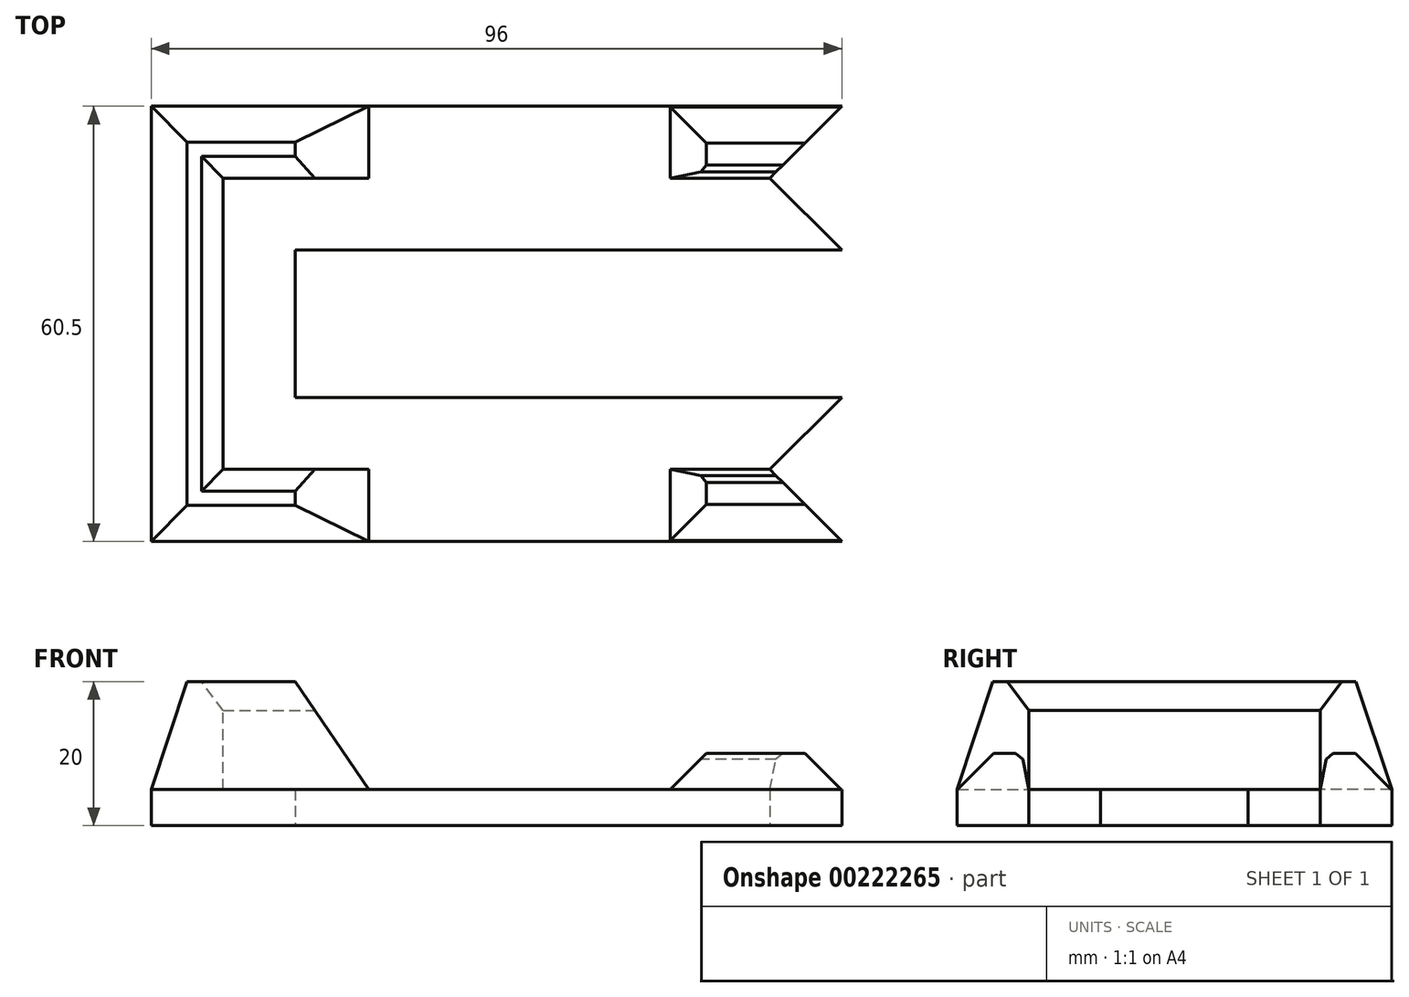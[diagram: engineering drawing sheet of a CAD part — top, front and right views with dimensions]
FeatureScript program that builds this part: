
annotation { "Feature Type Name" : "Feature", "Feature Type Description" : "" }
export const myFeature = defineFeature(function(context is Context, id is Id, definition is map)
    precondition{}
    {
        {
            var Q0;
            Q0=qCreatedBy(makeId("Top.planeOp"),FACE);
            var sketch = newSketch(context, id + "F0", { "sketchPlane" : qUnion([Q0])});
            skLineSegment(sketch, "E0.bottom", {"start": v(76, -20.25) * mm, "end": v(-76, -20.25) * mm, "construction": true});
            skLineSegment(sketch, "E0.top", {"start": v(76, 20.25) * mm, "end": v(-76, 20.25) * mm, "construction": true});
            skLineSegment(sketch, "E0.left", {"start": v(76, -20.25) * mm, "end": v(76, 20.25) * mm, "construction": true});
            skLineSegment(sketch, "E0.right", {"start": v(-76, -20.25) * mm, "end": v(-76, 20.25) * mm, "construction": true});
            skPoint(sketch, "E0.middle", {"position": v(0, 0) * mm});
            skLineSegment(sketch, "E1.bottom", {"start": v(86, -30.25) * mm, "end": v(-86, -30.25) * mm});
            skLineSegment(sketch, "E1.top", {"start": v(86, 30.25) * mm, "end": v(-86, 30.25) * mm});
            skLineSegment(sketch, "E1.left", {"start": v(86, -30.25) * mm, "end": v(86, 30.25) * mm});
            skLineSegment(sketch, "E1.right", {"start": v(-86, -30.25) * mm, "end": v(-86, 30.25) * mm});
            skSolve(sketch);
        }
        {
            var Q0;
            Q0=qCreatedBy(makeId("Top.planeOp"),FACE);
            cPlane(context, id + "F1", {"entities" : qUnion([Q0]), "cplaneType" : CPlaneType.OFFSET, "offset" : 15 * mm, "width" : 150 * mm, "height" : 150 * mm});
        }
        {
            var Q0;
            Q0=qCreatedBy(id+"F1.planeOp",FACE);
            var sketch = newSketch(context, id + "F2", { "sketchPlane" : qUnion([Q0])});
            skPoint(sketch, "E2.0", {"position": v(-86, -30.25) * mm});
            skPoint(sketch, "E3.0", {"position": v(-76, -20.25) * mm});
            skLineSegment(sketch, "E4", {"start": v(-76, 0) * mm, "end": v(-76, -20.25) * mm});
            skLineSegment(sketch, "E5", {"start": v(-76, -20.25) * mm, "end": v(-86, -30.25) * mm, "construction": true});
            skPoint(sketch, "E6", {"position": v(-81, -25.25) * mm});
            skLineSegment(sketch, "E7", {"start": v(-76, 0) * mm, "end": v(-81, 0) * mm});
            skLineSegment(sketch, "E8", {"start": v(-81, 0) * mm, "end": v(-81, -25.25) * mm});
            skLineSegment(sketch, "E9", {"start": v(-76, -20.25) * mm, "end": v(-66, -20.25) * mm});
            skLineSegment(sketch, "E10", {"start": v(-66, -20.25) * mm, "end": v(-66, -25.25) * mm});
            skLineSegment(sketch, "E11", {"start": v(-66, -25.25) * mm, "end": v(-81, -25.25) * mm});
            skSolve(sketch);
        }
        {
            var Q0;
            Q0=qCreatedBy(makeId("Top.planeOp"),FACE);
            var sketch = newSketch(context, id + "F3", { "sketchPlane" : qUnion([Q0])});
            skPoint(sketch, "E12.0", {"position": v(-86, -30.25) * mm});
            skPoint(sketch, "E13.0", {"position": v(-76, -20.25) * mm});
            skLineSegment(sketch, "E14", {"start": v(-86, -30.25) * mm, "end": v(-86, 0) * mm});
            skLineSegment(sketch, "E15", {"start": v(-86, 0) * mm, "end": v(-76, 0) * mm});
            skLineSegment(sketch, "E16", {"start": v(-76, 0) * mm, "end": v(-76, -20.25) * mm});
            skLineSegment(sketch, "E17", {"start": v(-76, -20.25) * mm, "end": v(-86, -30.25) * mm, "construction": true});
            skLineSegment(sketch, "E18.MirrorCS", {"start": v(-55.75, -20.25) * mm, "end": v(-76, -20.25) * mm});
            skLineSegment(sketch, "E19.MirrorCS", {"start": v(-86, -30.25) * mm, "end": v(-55.75, -30.25) * mm});
            skLineSegment(sketch, "E20.MirrorCS", {"start": v(-55.75, -30.25) * mm, "end": v(-55.75, -20.25) * mm});
            skLineSegment(sketch, "E21", {"start": v(0, 0) * mm, "end": v(-88.2, 0) * mm, "construction": true});
            skSolve(sketch);
        }
        {
            var Q0;
            Q0=makeQuery(id+"F0.imprint","IMPRINT",FACE,{"disambiguationData":[TD([[makeQuery(id+"F0.imprint","IMPRINT",EDGE,{"derivedFrom":sQuery(id+"F0.wireOp",EDGE,"E1.bottom")}),-1.0]])]});
            extrude(context, id + "F4", {"entities" : qUnion([Q0]), "oppositeDirection" : true, "depth" : 5 * mm});
        }
        {
            var Q1;
            Q1=makeQuery(id+"F3.imprint","IMPRINT",FACE,{"disambiguationData":[TD([[makeQuery(id+"F3.imprint","IMPRINT",EDGE,{"derivedFrom":sQuery(id+"F3.wireOp",EDGE,"E14")}),-1.0]])]});
            var Q2;
            Q2=makeQuery(id+"F2.imprint","IMPRINT",FACE,{"disambiguationData":[TD([[makeQuery(id+"F2.imprint","IMPRINT",EDGE,{"derivedFrom":sQuery(id+"F2.wireOp",EDGE,"E4")}),-1.0]])]});
            loft(context, id + "F5", {"operationType" : NewBodyOperationType.ADD, "sheetProfilesArray" : [{ "sheetProfileEntities" : qUnion([Q1]) }, { "sheetProfileEntities" : qUnion([Q2]) }]});
        }
        {
            var Q0;
            Q0=makeQuery(id+"F5.opLoft","MID_CAP_EDGE",EDGE,{"disambiguationData":[OSD([sQuery(id+"F2.wireOp",EDGE,"E4"),sQuery(id+"F2.wireOp",EDGE,"E7"),sQuery(id+"F2.wireOp",EDGE,"E9")])],"capPos":1.0});
            var Q1;
            Q1=makeQuery(id+"F5.opLoft","MID_CAP_EDGE",EDGE,{"disambiguationData":[OSD([sQuery(id+"F2.wireOp",EDGE,"E4"),sQuery(id+"F2.wireOp",EDGE,"E9"),sQuery(id+"F2.wireOp",EDGE,"E10")])],"capPos":1.0});
            chamfer(context, id + "F6", {"entities" : qUnion([Q0, Q1]), "chamferType" : ChamferType.TWO_OFFSETS, "width1" : 3 * mm, "oppositeDirection" : false, "width2" : 4 * mm, "tangentPropagation" : true});
        }
        {
            var Q0;
            Q0=makeQuery(id+"F4.opExtrude","SWEPT_BODY",BODY,{"disambiguationData":[OSD([sQuery(id+"F0.wireOp",EDGE,"E1.bottom"),sQuery(id+"F0.wireOp",EDGE,"E1.top"),sQuery(id+"F0.wireOp",EDGE,"E1.left"),sQuery(id+"F0.wireOp",EDGE,"E1.right")])]});
            var Q1;
            Q1=qCreatedBy(makeId("Right.planeOp"),FACE);
            mirror(context, id + "F7", {"operationType" : NewBodyOperationType.ADD, "entities" : qUnion([Q0]), "mirrorPlane" : qUnion([Q1])});
        }
        {
            var Q0;
            Q0=makeQuery(id+"F0.imprint","IMPRINT",FACE,{"disambiguationData":[TD([[makeQuery(id+"F0.imprint","IMPRINT",EDGE,{"derivedFrom":sQuery(id+"F0.wireOp",EDGE,"E1.bottom")}),-1.0]])]});
            var sketch = newSketch(context, id + "F8", { "sketchPlane" : qUnion([Q0])});
            skLineSegment(sketch, "E22", {"start": v(0, 45.4) * mm, "end": v(0, -36.03) * mm, "construction": true});
            skLineSegment(sketch, "E23", {"start": v(0, -20.25) * mm, "end": v(13.82, -20.25) * mm});
            skLineSegment(sketch, "E24", {"start": v(13.82, -20.25) * mm, "end": v(13.82, -30.13) * mm});
            skLineSegment(sketch, "E25", {"start": v(13.82, -30.13) * mm, "end": v(0, -30.13) * mm});
            skLineSegment(sketch, "E26.MirrorCS", {"start": v(-13.82, -30.13) * mm, "end": v(0, -30.13) * mm});
            skLineSegment(sketch, "E27.MirrorCS", {"start": v(0, -20.25) * mm, "end": v(-13.82, -20.25) * mm});
            skLineSegment(sketch, "E28.MirrorCS", {"start": v(-13.82, -20.25) * mm, "end": v(-13.82, -30.13) * mm});
            skSolve(sketch);
        }
        {
            var Q0;
            Q0=qSketchRegion(id+"F8",true);
            extrude(context, id + "F9", {"entities" : qUnion([Q0]), "operationType" : NewBodyOperationType.ADD, "depth" : 5 * mm});
        }
        {
            var Q0;
            Q0=makeQuery(id+"F9.opExtrude","CAP_EDGE",EDGE,{"disambiguationData":[OSD([sQuery(id+"F8.wireOp",EDGE,"E24")])],"isStart":false});
            var Q1;
            Q1=makeQuery(id+"F9.opExtrude","CAP_EDGE",EDGE,{"disambiguationData":[OSD([sQuery(id+"F8.wireOp",EDGE,"E25"),sQuery(id+"F8.wireOp",EDGE,"E26.MirrorCS")])],"isStart":false});
            var Q2;
            Q2=makeQuery(id+"F9.opExtrude","CAP_EDGE",EDGE,{"disambiguationData":[OSD([sQuery(id+"F8.wireOp",EDGE,"E28.MirrorCS")])],"isStart":false});
            chamfer(context, id + "F10", {"entities" : qUnion([Q0, Q1, Q2]), "width" : 5 * mm, "tangentPropagation" : true});
        }
        {
            var Q0;
            Q0=makeQuery(id+"F9.opExtrude","CAP_EDGE",EDGE,{"disambiguationData":[OSD([sQuery(id+"F8.wireOp",EDGE,"E23"),sQuery(id+"F8.wireOp",EDGE,"E27.MirrorCS")])],"isStart":false});
            chamfer(context, id + "F11", {"entities" : qUnion([Q0]), "chamferType" : ChamferType.TWO_OFFSETS, "width1" : 5 * mm, "oppositeDirection" : false, "width2" : 1 * mm, "tangentPropagation" : true});
        }
        {
            var Q0;
            {var subQ0=sQuery(id+"F8.wireOp",EDGE,"E27.MirrorCS");var subQ1=sQuery(id+"F8.wireOp",EDGE,"E23");Q0=makeQuery(id+"F11.opChamfer","BLEND_EDGE",EDGE,{"blendedFrom":[makeQuery(id+"F9.opExtrude","CAP_EDGE",EDGE,{"disambiguationData":[OSD([subQ1,subQ0])],"isStart":false}),makeQuery(id+"F9.opExtrude","CAP_FACE",FACE,{"disambiguationData":[OSD([subQ1,sQuery(id+"F8.wireOp",EDGE,"E24"),sQuery(id+"F8.wireOp",EDGE,"E25"),subQ0,sQuery(id+"F8.wireOp",EDGE,"E28.MirrorCS"),sQuery(id+"F8.wireOp",EDGE,"E26.MirrorCS")])],"isStart":false})],"blendedInto":[makeQuery(id+"F9.opExtrude","CAP_FACE",FACE,{"disambiguationData":[OSD([subQ1,sQuery(id+"F8.wireOp",EDGE,"E24"),sQuery(id+"F8.wireOp",EDGE,"E25"),subQ0,sQuery(id+"F8.wireOp",EDGE,"E28.MirrorCS"),sQuery(id+"F8.wireOp",EDGE,"E26.MirrorCS")])],"isStart":false})]});}
            chamfer(context, id + "F12", {"entities" : qUnion([Q0]), "width" : 1 * mm, "tangentPropagation" : true});
        }
        {
            var Q0;
            Q0=makeQuery(id+"F4.opExtrude","SWEPT_BODY",BODY,{"disambiguationData":[OSD([sQuery(id+"F0.wireOp",EDGE,"E1.bottom"),sQuery(id+"F0.wireOp",EDGE,"E1.top"),sQuery(id+"F0.wireOp",EDGE,"E1.left"),sQuery(id+"F0.wireOp",EDGE,"E1.right")])]});
            var Q1;
            Q1=qCreatedBy(makeId("Front.planeOp"),FACE);
            mirror(context, id + "F13", {"operationType" : NewBodyOperationType.ADD, "entities" : qUnion([Q0]), "mirrorPlane" : qUnion([Q1])});
        }
        {
            var Q0;
            Q0=qCreatedBy(makeId("Top.planeOp"),FACE);
            var sketch = newSketch(context, id + "F14", { "sketchPlane" : qUnion([Q0])});
            skLineSegment(sketch, "E29.bottom", {"start": v(66, -10.25) * mm, "end": v(-66, -10.25) * mm});
            skLineSegment(sketch, "E29.top", {"start": v(66, 10.25) * mm, "end": v(-66, 10.25) * mm});
            skLineSegment(sketch, "E29.left", {"start": v(66, -10.25) * mm, "end": v(66, 10.25) * mm});
            skLineSegment(sketch, "E29.right", {"start": v(-66, -10.25) * mm, "end": v(-66, 10.25) * mm});
            skPoint(sketch, "E29.middle", {"position": v(0, 0) * mm});
            skLineSegment(sketch, "E30.0", {"start": v(-76, -20.25) * mm, "end": v(-76, 20.25) * mm, "construction": true});
            skLineSegment(sketch, "E31.0", {"start": v(76, 20.25) * mm, "end": v(-76, 20.25) * mm, "construction": true});
            skSolve(sketch);
        }
        {
            var Q0;
            Q0=qSketchRegion(id+"F14",true);
            extrude(context, id + "F15", {"entities" : qUnion([Q0]), "operationType" : NewBodyOperationType.REMOVE, "endBound" : BoundingType.SYMMETRIC, "depth" : 25 * mm});
        }
        {
            var Q0;
            Q0=qCreatedBy(makeId("Top.planeOp"),FACE);
            var sketch = newSketch(context, id + "F16", { "sketchPlane" : qUnion([Q0])});
            skLineSegment(sketch, "E32.0", {"start": v(76, 20.25) * mm, "end": v(-76, 20.25) * mm, "construction": true});
            skLineSegment(sketch, "E32.1", {"start": v(-66, 10.25) * mm, "end": v(66, 10.25) * mm, "construction": true});
            skLineSegment(sketch, "E32.2", {"start": v(86, 30.25) * mm, "end": v(-86, 30.25) * mm, "construction": true});
            skPoint(sketch, "E32.3", {"position": v(0, 20.25) * mm});
            skLineSegment(sketch, "E33", {"start": v(0, 20.25) * mm, "end": v(18.64, 1.6) * mm});
            skLineSegment(sketch, "E34", {"start": v(18.64, 1.6) * mm, "end": v(18.64, -1.6) * mm});
            skLineSegment(sketch, "E35", {"start": v(18.64, -1.6) * mm, "end": v(0, -20.25) * mm});
            skLineSegment(sketch, "E36", {"start": v(0, -20.25) * mm, "end": v(26.9, -47.14) * mm});
            skLineSegment(sketch, "E37", {"start": v(26.9, -47.14) * mm, "end": v(91.07, -47.14) * mm});
            skLineSegment(sketch, "E38", {"start": v(91.07, -47.14) * mm, "end": v(91.07, 44.05) * mm});
            skLineSegment(sketch, "E39", {"start": v(91.07, 44.05) * mm, "end": v(23.8, 44.05) * mm});
            skLineSegment(sketch, "E40", {"start": v(23.8, 44.05) * mm, "end": v(0, 20.25) * mm});
            skSolve(sketch);
        }
        {
            var Q0;
            {var subQ5=sQuery(id+"F16.wireOp",EDGE,"E33");Q0=makeQuery(id+"F16.imprint","IMPRINT",FACE,{"disambiguationData":[TD([[makeQuery(id+"F16.imprint","IMPRINT",EDGE,{"derivedFrom":subQ5}),1.0]])]});}
            var Q1;
            {var subQ1=sQuery(id+"F16.wireOp",EDGE,"E37");Q1=makeQuery(id+"F16.imprint","IMPRINT",FACE,{"disambiguationData":[TD([[makeQuery(id+"F16.imprint","IMPRINT",EDGE,{"derivedFrom":subQ1}),1.0]])]});}
            extrude(context, id + "F17", {"entities" : qUnion([Q0, Q1]), "depth" : 25 * mm, "hasSecondDirection" : true, "secondDirectionOppositeDirection" : true, "secondDirectionDepth" : 25 * mm});
        }
        {
            var Q0;
            Q0=makeQuery(id+"F17.opExtrude","SWEPT_BODY",BODY,{"disambiguationData":[OSD([sQuery(id+"F16.wireOp",EDGE,"E33"),sQuery(id+"F16.wireOp",EDGE,"E34"),sQuery(id+"F16.wireOp",EDGE,"E35"),sQuery(id+"F16.wireOp",EDGE,"E36"),sQuery(id+"F16.wireOp",EDGE,"E37"),sQuery(id+"F16.wireOp",EDGE,"E38"),sQuery(id+"F16.wireOp",EDGE,"E39"),sQuery(id+"F16.wireOp",EDGE,"E40")])]});
            var Q1;
            Q1=makeQuery(id+"F4.opExtrude","SWEPT_BODY",BODY,{"disambiguationData":[OSD([sQuery(id+"F0.wireOp",EDGE,"E1.bottom"),sQuery(id+"F0.wireOp",EDGE,"E1.top"),sQuery(id+"F0.wireOp",EDGE,"E1.left"),sQuery(id+"F0.wireOp",EDGE,"E1.right")])]});
            booleanBodies(context, id + "F18", {"operationType" : BooleanOperationType.SUBTRACTION, "tools" : qUnion([Q0]), "targets" : qUnion([Q1])});
        }
    });
